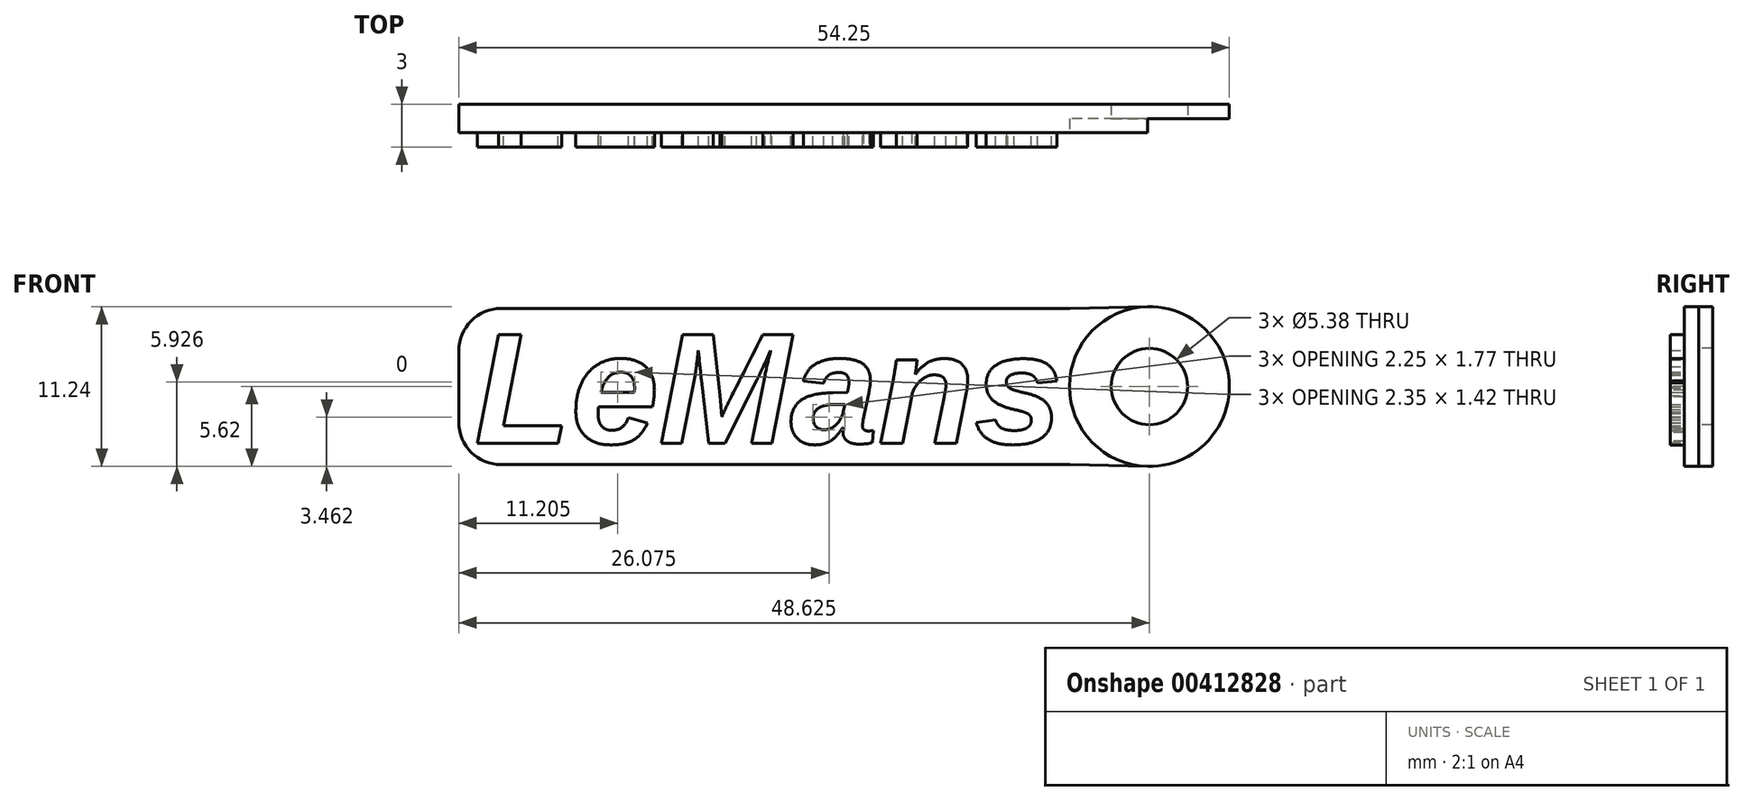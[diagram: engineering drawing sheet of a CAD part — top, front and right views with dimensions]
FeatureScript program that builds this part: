
annotation { "Feature Type Name" : "Feature", "Feature Type Description" : "" }
export const myFeature = defineFeature(function(context is Context, id is Id, definition is map)
    precondition{}
    {
        {
            var Q0;
            Q0=qCreatedBy(makeId("Front.planeOp"),FACE);
            var sketch = newSketch(context, id + "F0", { "sketchPlane" : qUnion([Q0])});
            skText(sketch, "E0", { "text": "LeMans", "fontName": "Arimo-BoldItalic.ttf"});
            const initialGuessF0  = {"E0": [-0.02088, -0.008, 1, 0, 0.008]};
            skSetInitialGuess(sketch, initialGuessF0);
            skSolve(sketch);
        }
        {
            var Q0;
            Q0=qSketchRegion(id+"F0",true);
            extrude(context, id + "F1", {"entities" : qUnion([Q0]), "depth" : 1 * mm});
        }
        {
            var Q0;
            Q0=qCreatedBy(makeId("Front.planeOp"),FACE);
            var sketch = newSketch(context, id + "F2", { "sketchPlane" : qUnion([Q0])});
            skLineSegment(sketch, "E1", {"start": v(21, -9.5) * mm, "end": v(-22, -9.5) * mm});
            skLineSegment(sketch, "E2", {"start": v(-22, 1.5) * mm, "end": v(21, 1.5) * mm});
            skLineSegment(sketch, "E3", {"start": v(21, -9.5) * mm, "end": v(21, 1.5) * mm, "construction": true});
            skLineSegment(sketch, "E4", {"start": v(-22, -9.5) * mm, "end": v(-22, 1.5) * mm});
            skCircle(sketch, "E5", {"center": v(26.63, -4) * mm, "radius": 5.62 * mm});
            skLineSegment(sketch, "E6", {"start": v(21, -4) * mm, "end": v(67.35, -4) * mm, "construction": true});
            skPoint(sketch, "E6.endSnap0", {"position": v(21, -4) * mm});
            skLineSegment(sketch, "E7", {"start": v(21, 1.5) * mm, "end": v(26.5, 1.62) * mm});
            skLineSegment(sketch, "E8", {"start": v(26.5, -9.62) * mm, "end": v(21, -9.5) * mm});
            skCircle(sketch, "E9", {"center": v(26.63, -4) * mm, "radius": 2.69 * mm});
            skSolve(sketch);
        }
        {
            var Q0;
            Q0=qSketchRegion(id+"F2",true);
            extrude(context, id + "F3", {"entities" : qUnion([Q0]), "oppositeDirection" : true, "depth" : 2 * mm});
        }
        {
            var Q0;
            Q0=makeQuery(id+"F3.opExtrude","SWEPT_EDGE",EDGE,{"disambiguationData":[OSD([sQuery(id+"F2.wireOp",EDGE,"E2"),sQuery(id+"F2.wireOp",EDGE,"E4")])]});
            var Q1;
            Q1=makeQuery(id+"F3.opExtrude","SWEPT_EDGE",EDGE,{"disambiguationData":[OSD([sQuery(id+"F2.wireOp",EDGE,"E1"),sQuery(id+"F2.wireOp",EDGE,"E4")])]});
            var Q2;
            Q2=makeQuery(id+"F3.opExtrude","SWEPT_EDGE",EDGE,{"disambiguationData":[OSD([sQuery(id+"F2.wireOp",EDGE,"E1"),sQuery(id+"F2.wireOp",EDGE,"E8")])]});
            var Q3;
            Q3=makeQuery(id+"F3.opExtrude","SWEPT_EDGE",EDGE,{"disambiguationData":[OSD([sQuery(id+"F2.wireOp",EDGE,"E2"),sQuery(id+"F2.wireOp",EDGE,"E7")])]});
            fillet(context, id + "F4", {"entities" : qUnion([Q0, Q1, Q2, Q3]), "radius" : 3 * mm, "tangentPropagation" : true, "allowEdgeOverflow" : false});
        }
        {
            var Q0;
            Q0=makeQuery(id+"F3.opExtrude","CAP_FACE",FACE,{"disambiguationData":[OSD([sQuery(id+"F2.wireOp",EDGE,"E1"),sQuery(id+"F2.wireOp",EDGE,"E2"),sQuery(id+"F2.wireOp",EDGE,"E4"),sQuery(id+"F2.wireOp",EDGE,"E5"),sQuery(id+"F2.wireOp",EDGE,"E7"),sQuery(id+"F2.wireOp",EDGE,"E8"),sQuery(id+"F2.wireOp",EDGE,"E9")])],"isStart":true});
            var sketch = newSketch(context, id + "F5", { "sketchPlane" : qUnion([Q0])});
            skCircle(sketch, "E10", {"center": v(26.63, -4) * mm, "radius": 5.62 * mm});
            skSolve(sketch);
        }
        {
            var Q0;
            Q0=qSketchRegion(id+"F5",true);
            extrude(context, id + "F6", {"entities" : qUnion([Q0]), "operationType" : NewBodyOperationType.REMOVE, "oppositeDirection" : true, "depth" : 1 * mm});
        }
    });
